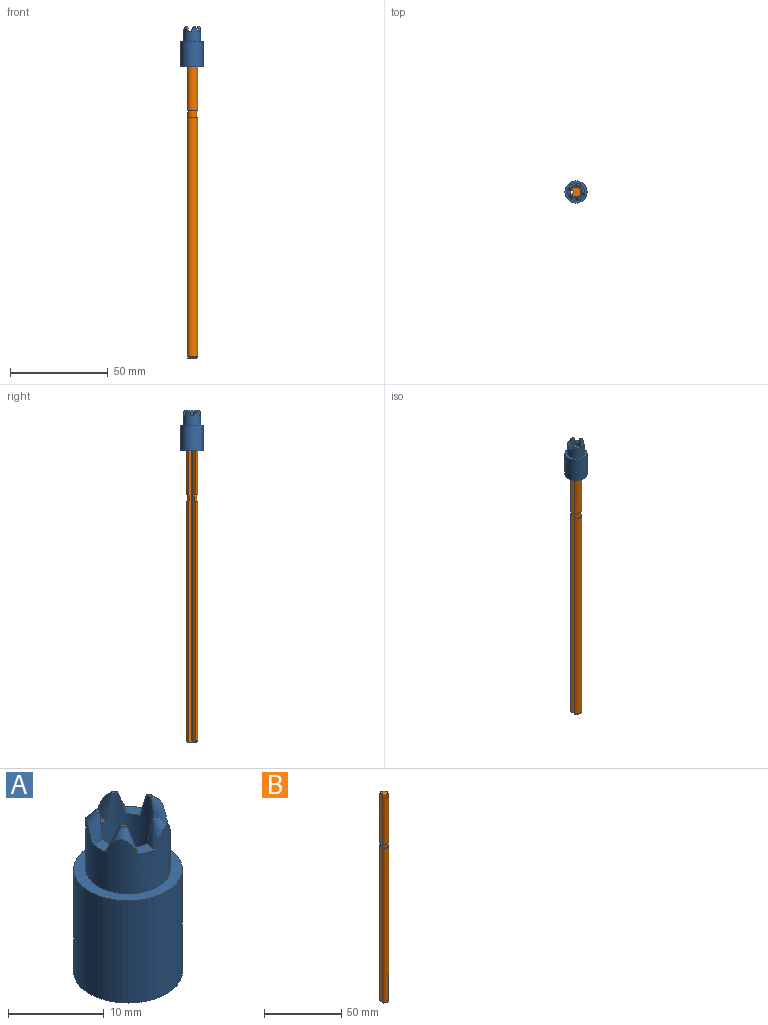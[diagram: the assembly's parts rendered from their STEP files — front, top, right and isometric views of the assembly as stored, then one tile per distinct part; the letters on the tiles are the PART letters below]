
ASSEMBLY  parts=2 mates=1
PART A: 20 faces, bbox 11.7x11.7x21.3 mm
  f0: cone r=1.8mm half-angle=24.8deg, axis (0.34,0,-0.94), area 9.2mm2, adj f1,f2,f3,f4,f16
  f1: plane 0.98x0.75mm, normal (0,0,1), area 0.2mm2, adj f0,f2
  f2: cylinder r=3.04mm len=20.85mm, axis (0,0,-1), area 363.1mm2, adj f0,f1,f4,f5,f6,f7,f8,f9
  f3: cylinder r=4.4mm len=8.8mm, axis (0,0,-1), area 159.2mm2, adj f0,f4,f6,f7,f9,f10,f12,f13
  f4: plane 2.34x2.24mm, normal (0,0,1), area 2.3mm2, adj f0,f2,f3,f6
  f5: plane 0.98x0.84mm, normal (0,0,1), area 0.2mm2, adj f2,f6
  f6: cone r=1.8mm half-angle=24.8deg, axis (0.11,0.33,-0.94), area 9.2mm2, adj f2,f3,f4,f5,f7
  f7: plane 2.22x1.93mm, normal (0,0,1), area 2.3mm2, adj f2,f3,f6,f9
  f8: plane 0.96x0.91mm, normal (0,0,1), area 0.2mm2, adj f2,f9
  f9: cone r=1.8mm half-angle=24.8deg, axis (-0.28,0.2,-0.94), area 9.2mm2, adj f2,f3,f7,f8,f10
  f10: plane 2.02x1.55mm, normal (0,0,1), area 2.3mm2, adj f2,f3,f9,f12
  f11: plane 0.96x0.91mm, normal (0,0,1), area 0.2mm2, adj f2,f12
  f12: cone r=1.8mm half-angle=24.8deg, axis (-0.28,-0.2,-0.94), area 9.2mm2, adj f2,f3,f10,f11,f13
  f13: plane 2.22x1.93mm, normal (0,0,1), area 2.3mm2, adj f2,f3,f12,f14
  f14: cone r=1.8mm half-angle=24.8deg, axis (0.11,-0.33,-0.94), area 9.2mm2, adj f2,f3,f13,f15,f16
  f15: plane 0.98x0.84mm, normal (0,0,1), area 0.2mm2, adj f2,f14
  f16: plane 2.34x2.24mm, normal (0,0,1), area 2.3mm2, adj f0,f2,f3,f14
  f17: cylinder r=5.68mm len=13.05mm, axis (0,0,1), area 465.3mm2, adj f18,f19
  f18: plane 11.35x11.35mm, normal (0,0,-1), area 72.1mm2, adj f2,f17
  f19: plane 11.35x11.35mm, normal (0,0,1), area 40.4mm2, adj f3,f17
PART B: 12 faces, bbox 5.6x5.9x165 mm
  f0: cylinder r=2.95mm len=122.55mm, axis (0,0,-1), area 1867.7mm2, adj f1,f3,f7,f11
  f1: plane 165.02x1.36mm, normal (-0.71,0.71,0), area 309.7mm2, adj f0,f2,f4,f5,f6,f7,f8,f9
  f2: cylinder r=2.95mm len=37.05mm, axis (0,0,-1), area 564.7mm2, adj f1,f3,f8,f10
  f3: plane 165.02x1.36mm, normal (-0.71,-0.71,0), area 309.7mm2, adj f0,f2,f4,f5,f6,f7,f8,f9
  f4: cylinder r=0.3mm len=165mm, axis (0,0,-1), area 77.8mm2, adj f1,f3,f5,f6
  f5: plane 5.09x4.75mm, normal (0,0,1), area 18.2mm2, adj f1,f3,f4,f8
  f6: plane 4.69x4.41mm, normal (0,0,-1), area 15.6mm2, adj f1,f3,f4,f7
  f7: cone r=2.95mm half-angle=45deg, axis (0,0,1), area 11.7mm2, adj f0,f1,f3,f6
  f8: cone r=2.54mm half-angle=15deg, axis (0,0,-1), area 22.2mm2, adj f1,f2,f3,f5
  f9: cylinder r=2.4mm len=4.8mm, axis (0,0,-1), area 41.8mm2, adj f1,f3,f10,f11
  f10: plane 5.89x5.45mm, normal (0,0,-1), area 7.6mm2, adj f1,f2,f3,f9
  f11: plane 5.89x5.45mm, normal (0,0,1), area 7.6mm2, adj f0,f1,f3,f9
PLACE A at identity fixed
PLACE B t=(0,0,-162.15)mm
MATE fastened B.f0 <-> A.f2  axis (0,0,1) through (0,0,2.85)mm
